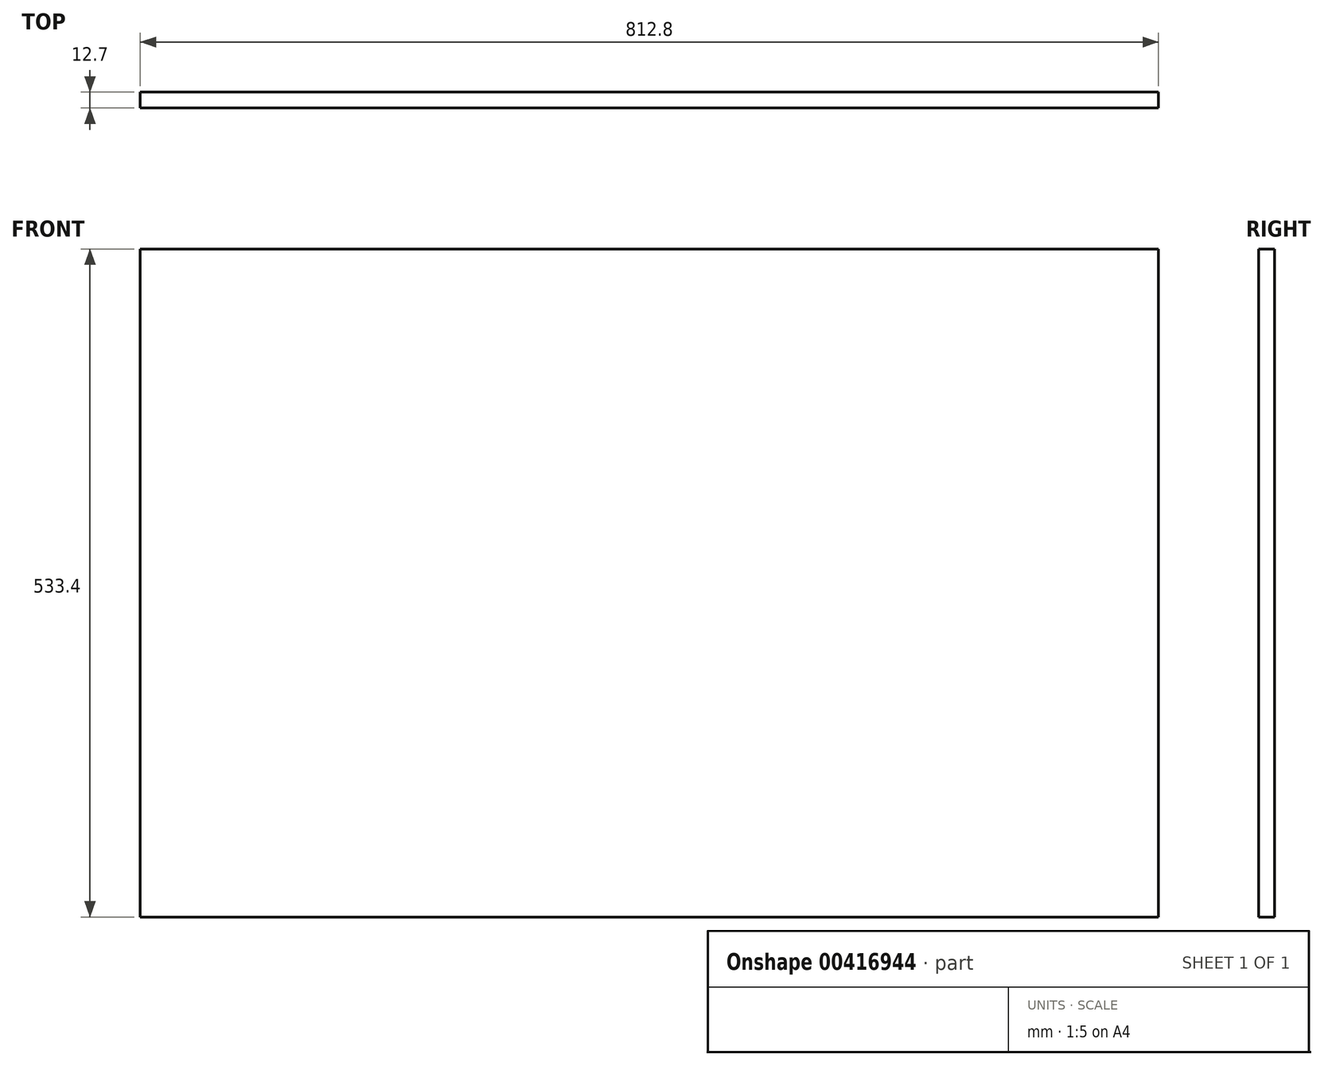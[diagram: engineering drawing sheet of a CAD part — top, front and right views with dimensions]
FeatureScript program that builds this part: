
annotation { "Feature Type Name" : "Feature", "Feature Type Description" : "" }
export const myFeature = defineFeature(function(context is Context, id is Id, definition is map)
    precondition{}
    {
        {
            var Q0;
            Q0=qCreatedBy(makeId("Front.planeOp"),FACE);
            var sketch = newSketch(context, id + "F0", { "sketchPlane" : qUnion([Q0])});
            skLineSegment(sketch, "E0.bottom", {"start": v(406.4, 266.7) * mm, "end": v(-406.4, 266.7) * mm});
            skLineSegment(sketch, "E0.top", {"start": v(406.4, -266.7) * mm, "end": v(-406.4, -266.7) * mm});
            skLineSegment(sketch, "E0.left", {"start": v(406.4, 266.7) * mm, "end": v(406.4, -266.7) * mm});
            skLineSegment(sketch, "E0.right", {"start": v(-406.4, 266.7) * mm, "end": v(-406.4, -266.7) * mm});
            skPoint(sketch, "E0.middle", {"position": v(0, 0) * mm});
            skSolve(sketch);
        }
        {
            var Q0;
            Q0=makeQuery(id+"F0.imprint","IMPRINT",FACE,{"disambiguationData":[TD([[makeQuery(id+"F0.imprint","IMPRINT",EDGE,{"derivedFrom":sQuery(id+"F0.wireOp",EDGE,"E0.bottom")}),1.0]])]});
            var Q1;
            Q1=sQuery(id+"F0.wireOp",EDGE,"E0.right");
            var Q2;
            Q2=sQuery(id+"F0.wireOp",EDGE,"E0.bottom");
            var Q3;
            Q3=sQuery(id+"F0.wireOp",EDGE,"E0.left");
            var Q4;
            Q4=sQuery(id+"F0.wireOp",EDGE,"E0.top");
            extrude(context, id + "F1", {"entities" : qUnion([Q0]), "surfaceEntities" : qUnion([Q1, Q2, Q3, Q4]), "depth" : 12.7 * mm});
        }
    });
